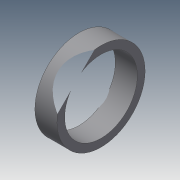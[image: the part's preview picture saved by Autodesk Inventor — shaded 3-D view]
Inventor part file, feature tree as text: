
AUTODESK INVENTOR PART (.ipt)
format: ipt  version: 2014 SP1 (Build 180222100, 222)  size: 230,400 bytes
history: native  units: in
note: dims shown in document units (in); Inventor stores cm internally (conversion verified against a paired STEP export)
features: extrude x4, sketch x3, pattern_circular x2
ambient origin geometry x8: Origin, YZ Plane, XZ Plane, XY Plane, X Axis, Y Axis, Z Axis, Center Point
bodies: Solid1 (feature_tree)
feature tree (9):
  extrude  "Extrusion1"  Depth=0.5in
  extrude  "Extrusion2"  Depth=1.5in
  extrude  "Extrusion3"  Depth=0.25in
  pattern_circular  "Circular Pattern1"  [2 undecoded]
  extrude  "Extrusion4"  Depth=0.25in
  pattern_circular  "Circular Pattern2"  [2 undecoded]
  sketch  "Sketch2"  dims[d0=4.0in d1=0.5in]
  sketch  "Sketch4"  dims[d2=0.77in d3=1.5in]
  sketch  "Sketch5"  dims[d4=2.0in d5=2.5in d6=3.0in d7=3.3in d17=0.25in d18=0.0in d19=4.0in d20=0.5in d21=0.77in d22=1.5in d23=2.0in d24=2.5in d25=3.0in d26=3.3in d27=0.14in d28=0.14in d29=0.14in d30=0.14in d31=0.14in d32=1.0in d33=0.0in d34=4.0in d35=0.5in d36=0.77in d37=1.5in d38=2.0in d39=2.5in d40=3.0in d41=3.3in d42=0.14in d43=0.14in d44=0.14in d45=0.14in d46=0.14in d47=0.25in d48=0.0in d49=3.1496in d50=360.0deg d53=0.0625in d54=0.25in d55=0.0in d56=3.1496in d57=360.0deg]
note: 4 required parameter values undecoded (feature->parameter linkage not recoverable at this tier; creation-order binding heuristic only, values carry confidence <= 0.55)
